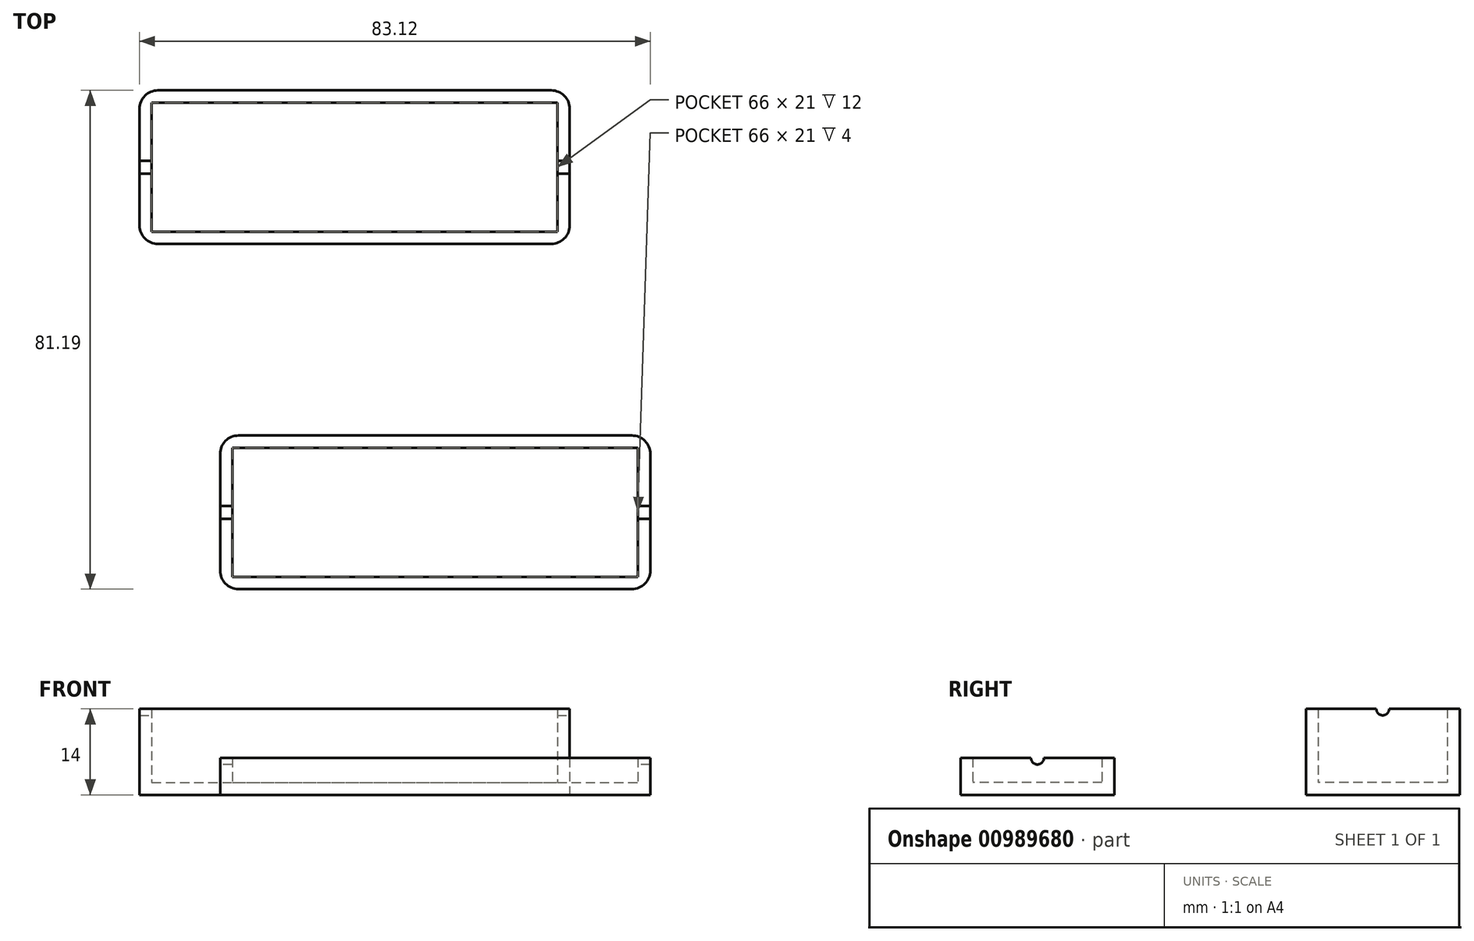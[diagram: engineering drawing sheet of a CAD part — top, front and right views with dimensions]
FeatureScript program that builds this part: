
annotation { "Feature Type Name" : "Feature", "Feature Type Description" : "" }
export const myFeature = defineFeature(function(context is Context, id is Id, definition is map)
    precondition{}
    {
        {
            var Q0;
            Q0=qCreatedBy(makeId("Top.planeOp"),FACE);
            var sketch = newSketch(context, id + "F0", { "sketchPlane" : qUnion([Q0])});
            skLineSegment(sketch, "E0.bottom", {"start": v(-67.06, 33.56) * mm, "end": v(-1.06, 33.56) * mm});
            skLineSegment(sketch, "E0.top", {"start": v(-67.06, 12.56) * mm, "end": v(-1.06, 12.56) * mm});
            skLineSegment(sketch, "E0.left", {"start": v(-67.06, 33.56) * mm, "end": v(-67.06, 12.56) * mm});
            skLineSegment(sketch, "E0.right", {"start": v(-1.06, 33.56) * mm, "end": v(-1.06, 12.56) * mm});
            skLineSegment(sketch, "E1.top", {"start": v(-67.06, 35.56) * mm, "end": v(-1.06, 35.56) * mm});
            skLineSegment(sketch, "E1.left", {"start": v(-67.06, 33.56) * mm, "end": v(-67.06, 35.56) * mm});
            skLineSegment(sketch, "E1.right", {"start": v(-1.06, 33.56) * mm, "end": v(-1.06, 35.56) * mm});
            skLineSegment(sketch, "E2.top", {"start": v(-67.06, 10.56) * mm, "end": v(-1.06, 10.56) * mm});
            skLineSegment(sketch, "E2.left", {"start": v(-67.06, 12.56) * mm, "end": v(-67.06, 10.56) * mm});
            skLineSegment(sketch, "E2.right", {"start": v(-1.06, 12.56) * mm, "end": v(-1.06, 10.56) * mm});
            skLineSegment(sketch, "E3.bottom", {"start": v(-67.06, 35.56) * mm, "end": v(-69.06, 35.56) * mm});
            skLineSegment(sketch, "E3.top", {"start": v(-67.06, 10.56) * mm, "end": v(-69.06, 10.56) * mm});
            skLineSegment(sketch, "E3.left", {"start": v(-67.06, 35.56) * mm, "end": v(-67.06, 10.56) * mm});
            skLineSegment(sketch, "E3.right", {"start": v(-69.06, 35.56) * mm, "end": v(-69.06, 10.56) * mm});
            skLineSegment(sketch, "E4.bottom", {"start": v(-1.06, 35.56) * mm, "end": v(0.94, 35.56) * mm});
            skLineSegment(sketch, "E4.top", {"start": v(-1.06, 10.56) * mm, "end": v(0.94, 10.56) * mm});
            skLineSegment(sketch, "E4.left", {"start": v(-1.06, 35.56) * mm, "end": v(-1.06, 10.56) * mm});
            skLineSegment(sketch, "E4.right", {"start": v(0.94, 35.56) * mm, "end": v(0.94, 10.56) * mm});
            skLineSegment(sketch, "E5.bottom", {"start": v(-53.94, -22.63) * mm, "end": v(12.06, -22.63) * mm});
            skLineSegment(sketch, "E5.top", {"start": v(-53.94, -43.63) * mm, "end": v(12.06, -43.63) * mm});
            skLineSegment(sketch, "E5.left", {"start": v(-53.94, -22.63) * mm, "end": v(-53.94, -43.63) * mm});
            skLineSegment(sketch, "E5.right", {"start": v(12.06, -22.63) * mm, "end": v(12.06, -43.63) * mm});
            skLineSegment(sketch, "E6.top", {"start": v(-53.94, -20.63) * mm, "end": v(12.06, -20.63) * mm});
            skLineSegment(sketch, "E6.left", {"start": v(-53.94, -22.63) * mm, "end": v(-53.94, -20.63) * mm});
            skLineSegment(sketch, "E6.right", {"start": v(12.06, -22.63) * mm, "end": v(12.06, -20.63) * mm});
            skLineSegment(sketch, "E7.top", {"start": v(-53.94, -45.63) * mm, "end": v(12.06, -45.63) * mm});
            skLineSegment(sketch, "E7.left", {"start": v(-53.94, -43.63) * mm, "end": v(-53.94, -45.63) * mm});
            skLineSegment(sketch, "E7.right", {"start": v(12.06, -43.63) * mm, "end": v(12.06, -45.63) * mm});
            skLineSegment(sketch, "E8.bottom", {"start": v(-53.94, -20.63) * mm, "end": v(-55.94, -20.63) * mm});
            skLineSegment(sketch, "E8.top", {"start": v(-53.94, -45.63) * mm, "end": v(-55.94, -45.63) * mm});
            skLineSegment(sketch, "E8.left", {"start": v(-53.94, -20.63) * mm, "end": v(-53.94, -45.63) * mm});
            skLineSegment(sketch, "E8.right", {"start": v(-55.94, -20.63) * mm, "end": v(-55.94, -45.63) * mm});
            skLineSegment(sketch, "E9.bottom", {"start": v(12.06, -20.63) * mm, "end": v(14.06, -20.63) * mm});
            skLineSegment(sketch, "E9.top", {"start": v(12.06, -45.63) * mm, "end": v(14.06, -45.63) * mm});
            skLineSegment(sketch, "E9.left", {"start": v(12.06, -20.63) * mm, "end": v(12.06, -45.63) * mm});
            skLineSegment(sketch, "E9.right", {"start": v(14.06, -20.63) * mm, "end": v(14.06, -45.63) * mm});
            skSolve(sketch);
        }
        {
            var Q0;
            Q0=makeQuery(id+"F0.imprint","IMPRINT",FACE,{"disambiguationData":[TD([[makeQuery(id+"F0.imprint","IMPRINT",EDGE,{"derivedFrom":sQuery(id+"F0.wireOp",EDGE,"E0.bottom")}),-1.0]])]});
            extrude(context, id + "F1", {"entities" : qUnion([Q0]), "depth" : 2 * mm, "offsetDistance" : 25 * mm});
        }
        {
            var Q0;
            Q0=makeQuery(id+"F0.imprint","IMPRINT",FACE,{"disambiguationData":[TD([[makeQuery(id+"F0.imprint","IMPRINT",EDGE,{"derivedFrom":sQuery(id+"F0.wireOp",EDGE,"E0.left")}),-1.0]])]});
            var Q1;
            Q1=makeQuery(id+"F0.imprint","IMPRINT",FACE,{"disambiguationData":[TD([[makeQuery(id+"F0.imprint","IMPRINT",EDGE,{"derivedFrom":sQuery(id+"F0.wireOp",EDGE,"E0.top")}),-1.0]])]});
            var Q2;
            Q2=makeQuery(id+"F0.imprint","IMPRINT",FACE,{"disambiguationData":[TD([[makeQuery(id+"F0.imprint","IMPRINT",EDGE,{"derivedFrom":sQuery(id+"F0.wireOp",EDGE,"E0.right")}),1.0]])]});
            var Q3;
            Q3=makeQuery(id+"F0.imprint","IMPRINT",FACE,{"disambiguationData":[TD([[makeQuery(id+"F0.imprint","IMPRINT",EDGE,{"derivedFrom":sQuery(id+"F0.wireOp",EDGE,"E0.bottom")}),1.0]])]});
            extrude(context, id + "F2", {"entities" : qUnion([Q0, Q1, Q2, Q3]), "operationType" : NewBodyOperationType.ADD, "depth" : 14 * mm, "offsetDistance" : 25 * mm});
        }
        {
            var Q0;
            Q0=makeQuery(id+"F2.opExtrude","SWEPT_FACE",FACE,{"disambiguationData":[OSD([sQuery(id+"F0.wireOp",EDGE,"E4.right")])]});
            var sketch = newSketch(context, id + "F3", { "sketchPlane" : qUnion([Q0])});
            skCircle(sketch, "E10", {"center": v(23.06, 14) * mm, "radius": 1.05 * mm});
            skSolve(sketch);
        }
        {
            var Q0;
            {var subQ0=sQuery(id+"F3.wireOp",EDGE,"E10");var subQ1=makeQuery(id+"F2.opExtrude","CAP_EDGE",EDGE,{"disambiguationData":[OSD([sQuery(id+"F0.wireOp",EDGE,"E4.right")])],"isStart":false});var subQ2=makeQuery(id+"F3.imprint","INTERSECT",VERTEX,{"disambiguationData":[OD(0.0)],"derivedFrom":[subQ1,subQ0]});Q0=makeQuery(id+"F3.imprint","IMPRINT",FACE,{"disambiguationData":[TD([[makeQuery(id+"F3.imprint","IMPRINT",EDGE,{"disambiguationData":[TD([[subQ2,1.0]])],"derivedFrom":subQ0}),1.0]])]});}
            extrude(context, id + "F4", {"entities" : qUnion([Q0]), "operationType" : NewBodyOperationType.REMOVE, "oppositeDirection" : true, "depth" : 80 * mm, "offsetDistance" : 25 * mm});
        }
        {
            var Q0;
            Q0=makeQuery(id+"F2.opExtrude","SWEPT_EDGE",EDGE,{"disambiguationData":[OSD([sQuery(id+"F0.wireOp",EDGE,"E3.bottom"),sQuery(id+"F0.wireOp",EDGE,"E3.right")])]});
            var Q1;
            Q1=makeQuery(id+"F2.opExtrude","SWEPT_EDGE",EDGE,{"disambiguationData":[OSD([sQuery(id+"F0.wireOp",EDGE,"E3.top"),sQuery(id+"F0.wireOp",EDGE,"E3.right")])]});
            var Q2;
            Q2=makeQuery(id+"F2.opExtrude","SWEPT_EDGE",EDGE,{"disambiguationData":[OSD([sQuery(id+"F0.wireOp",EDGE,"E4.bottom"),sQuery(id+"F0.wireOp",EDGE,"E4.right")])]});
            var Q3;
            Q3=makeQuery(id+"F2.opExtrude","SWEPT_EDGE",EDGE,{"disambiguationData":[OSD([sQuery(id+"F0.wireOp",EDGE,"E4.top"),sQuery(id+"F0.wireOp",EDGE,"E4.right")])]});
            fillet(context, id + "F5", {"entities" : qUnion([Q0, Q1, Q2, Q3]), "radius" : 3 * mm, "tangentPropagation" : true, "allowEdgeOverflow" : false});
        }
        {
            var Q0;
            Q0=makeQuery(id+"F0.imprint","IMPRINT",FACE,{"disambiguationData":[TD([[makeQuery(id+"F0.imprint","IMPRINT",EDGE,{"derivedFrom":sQuery(id+"F0.wireOp",EDGE,"E5.bottom")}),-1.0]])]});
            extrude(context, id + "F6", {"entities" : qUnion([Q0]), "depth" : 2 * mm, "offsetDistance" : 25 * mm});
        }
        {
            var Q0;
            Q0=makeQuery(id+"F0.imprint","IMPRINT",FACE,{"disambiguationData":[TD([[makeQuery(id+"F0.imprint","IMPRINT",EDGE,{"derivedFrom":sQuery(id+"F0.wireOp",EDGE,"E5.bottom")}),1.0]])]});
            var Q1;
            Q1=makeQuery(id+"F0.imprint","IMPRINT",FACE,{"disambiguationData":[TD([[makeQuery(id+"F0.imprint","IMPRINT",EDGE,{"derivedFrom":sQuery(id+"F0.wireOp",EDGE,"E5.left")}),-1.0]])]});
            var Q2;
            Q2=makeQuery(id+"F0.imprint","IMPRINT",FACE,{"disambiguationData":[TD([[makeQuery(id+"F0.imprint","IMPRINT",EDGE,{"derivedFrom":sQuery(id+"F0.wireOp",EDGE,"E5.top")}),-1.0]])]});
            var Q3;
            Q3=makeQuery(id+"F0.imprint","IMPRINT",FACE,{"disambiguationData":[TD([[makeQuery(id+"F0.imprint","IMPRINT",EDGE,{"derivedFrom":sQuery(id+"F0.wireOp",EDGE,"E5.right")}),1.0]])]});
            extrude(context, id + "F7", {"entities" : qUnion([Q0, Q1, Q2, Q3]), "operationType" : NewBodyOperationType.ADD, "depth" : 6 * mm, "offsetDistance" : 25 * mm});
        }
        {
            var Q0;
            Q0=makeQuery(id+"F7.opExtrude","SWEPT_EDGE",EDGE,{"disambiguationData":[OSD([sQuery(id+"F0.wireOp",EDGE,"E8.top"),sQuery(id+"F0.wireOp",EDGE,"E8.right")])]});
            var Q1;
            Q1=makeQuery(id+"F7.opExtrude","SWEPT_EDGE",EDGE,{"disambiguationData":[OSD([sQuery(id+"F0.wireOp",EDGE,"E8.bottom"),sQuery(id+"F0.wireOp",EDGE,"E8.right")])]});
            var Q2;
            Q2=makeQuery(id+"F7.opExtrude","SWEPT_EDGE",EDGE,{"disambiguationData":[OSD([sQuery(id+"F0.wireOp",EDGE,"E9.bottom"),sQuery(id+"F0.wireOp",EDGE,"E9.right")])]});
            var Q3;
            Q3=makeQuery(id+"F7.opExtrude","SWEPT_EDGE",EDGE,{"disambiguationData":[OSD([sQuery(id+"F0.wireOp",EDGE,"E9.top"),sQuery(id+"F0.wireOp",EDGE,"E9.right")])]});
            fillet(context, id + "F8", {"entities" : qUnion([Q0, Q1, Q2, Q3]), "radius" : 3 * mm, "tangentPropagation" : true, "allowEdgeOverflow" : false});
        }
        {
            var Q0;
            Q0=makeQuery(id+"F7.opExtrude","SWEPT_FACE",FACE,{"disambiguationData":[OSD([sQuery(id+"F0.wireOp",EDGE,"E8.right")])]});
            var sketch = newSketch(context, id + "F9", { "sketchPlane" : qUnion([Q0])});
            skCircle(sketch, "E11", {"center": v(33.13, 6) * mm, "radius": 1.05 * mm});
            skSolve(sketch);
        }
        {
            var Q0;
            {var subQ0=sQuery(id+"F9.wireOp",EDGE,"E11");var subQ1=makeQuery(id+"F7.opExtrude","CAP_EDGE",EDGE,{"disambiguationData":[OSD([sQuery(id+"F0.wireOp",EDGE,"E8.right")])],"isStart":false});var subQ2=makeQuery(id+"F9.imprint","INTERSECT",VERTEX,{"disambiguationData":[OD(0.0)],"derivedFrom":[subQ1,subQ0]});Q0=makeQuery(id+"F9.imprint","IMPRINT",FACE,{"disambiguationData":[TD([[makeQuery(id+"F9.imprint","IMPRINT",EDGE,{"disambiguationData":[TD([[subQ2,-1.0]])],"derivedFrom":subQ0}),1.0]])]});}
            extrude(context, id + "F10", {"entities" : qUnion([Q0]), "operationType" : NewBodyOperationType.REMOVE, "oppositeDirection" : true, "depth" : 80 * mm, "offsetDistance" : 25 * mm});
        }
    });
